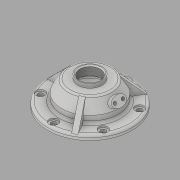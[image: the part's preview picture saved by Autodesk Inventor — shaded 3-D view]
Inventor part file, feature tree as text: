
AUTODESK INVENTOR PART (.ipt)
format: ipt  version: 2020 (Build 240168000, 168)  size: 345,600 bytes
history: native  units: mm
features: sketch x9, hole x4, thread x3, extrude x2, pattern_circular x2, plane x2, revolve x1
ambient origin geometry x8: Origin, YZ Plane, XZ Plane, XY Plane, X Axis, Y Axis, Z Axis, Center Point
bodies: Solid1 (feature_tree)
feature tree (23):
  revolve  "Revolution1"  [1 undecoded]
  extrude  "Extrusion1"  Depth=6.0mm
  hole  "Hole1"  [1 undecoded]
  hole  "Hole2"  [1 undecoded]
  pattern_circular  "Circular Pattern1"  Count=4  [1 undecoded]
  pattern_circular  "Circular Pattern2"  Angle=90.0deg  [1 undecoded]
  plane  "Work Plane1"
  sketch  "Sketch5"  dims[d9=11.0mm d10=40.0mm]
  sketch  "Sketch6"  dims[d11=30.0deg]
  plane  "Work Plane2"
  extrude  "Extrusion2"  Depth=2.0mm
  hole  "Hole3"  [1 undecoded]
  hole  "Hole4"  [1 undecoded]
  thread  "Thread1"  [1 undecoded]
  thread  "Thread2"  [1 undecoded]
  thread  "Thread3"  [1 undecoded]
  sketch  "Sketch1"  dims[d0=104.0mm d2=54.0mm]
  sketch  "Sketch2"  dims[d3=30.0mm d4=6.0mm]
  sketch  "Sketch3"  dims[d5=15.0mm d6=70.0mm]
  sketch  "Sketch4"  dims[d7=50.0mm d8=18.0mm]
  sketch  "Sketch7"  dims[d12=24.0mm]
  sketch  "Sketch8"  dims[d13=3.0mm]
  sketch  "Sketch9"  dims[d14=3.0mm d15=90.0deg d16=3.0mm d17=3.0mm d18=6.0mm d19=0.0mm d20=90.0mm d21=6.5mm d22=6.0mm d23=11.0mm d24=2.0mm d25=90.0deg d26=8.0mm d27=20.594885mm d28=90.0mm d29=4.0mm d30=6.0mm d31=11.0mm d32=2.0mm d33=90.0deg d34=8.0mm d35=20.594885mm d36=30.0mm d37=360.0deg d39=-1.5mm d40=5.0mm d41=0.0mm d43=12.0mm d44=18.0mm d45=10.0mm d46=4.0mm d47=6.0mm d48=4.0mm d49=2.0mm d50=90.0deg d51=8.0mm d52=20.594885mm d53=30.0mm d54=35.0mm d55=25.4mm d56=6.0mm d57=28.0mm d58=2.0mm d59=90.0deg d60=8.0mm d61=20.594885mm d62=60.0mm d63=360.0deg d65=9.7mm d66=0.0mm d67=5.0mm d68=0.0mm d69=5.0mm d70=0.0mm]
note: 10 required parameter values undecoded (feature->parameter linkage not recoverable at this tier; creation-order binding heuristic only, values carry confidence <= 0.55)